# Revit family: ATAG_CV_ketel_Q51_en_Q60_solo
name_source: partatom
category: Mechanical Equipment
revit_build: Autodesk Revit 2014 (Build: 20130308_1515(x64)
units: mm (PartAtom-declared; Revit-internal decimal feet)

## types (2) — shared parameters
BCB_I BaseKeynote = 56.10.10.13.01
BCB_I Beschermingsgraad vlgs. EN 60529 = IPX0D
BCB_I Beschikbare opvoerhoogte pomp CV = 0.00 Pa
BCB_I Gaskeur HR Top = HR Top
BCB_I Gaskeur SV_gaskeurlabel schone verbranding = SV
BCB_I Gewicht (leeg) = 64
BCB_I Rendement volgens EN677 (36/30°C deellast, onderw.) = 109,3
BCB_I Rendement volgens EN677 (80/60°C vollast, onderw.) = 97,3
BCB_V Aansluitdiameter CVr = 35 mm
BCB_V Aansluitdiameter CVv = 35 mm
BCB_V Aansluitdiameter condensafvoer = 24 mm
BCB_V Aansluitdiameter gas = 20 mm
BCB_V Aansluitdiameter luchttoevoer = 80 mm  [stored 0.262467 ft]
BCB_V Aansluitdiameter rookgasafvoer = 80 mm  [stored 0.262467 ft]
BCB_V Luchtinlaat_materiaal = BE Kunststof_zwart
BCB_c1 Debiet = 0 CFM
BCB_c1 Omschrijving = c1_Rookgasafvoer
BCB_c1 Straal = 40 mm  [stored 0.131234 ft]
BCB_c2 Omschrijving = c2_Elektrische voeding
BCB_c3 Debiet = 0.0000 L/s
BCB_c3 Energie_inhoud gas = 0 kWh
BCB_c3 Omschrijving = c3_Gasaansluiting
BCB_c3 Straal = 10 mm  [stored 0.0328084 ft]
BCB_c3 Vermogen = 0 kW
BCB_c4 Omschrijving = c4_CV-toevoer
BCB_c4 Straal = 18 mm  [stored 0.0590551 ft]
BCB_c5 Omschrijving = c5_CV-retour
BCB_c5 Straal = 18 mm  [stored 0.0590551 ft]
BCB_c6 Omschrijving = c6_Condensafvoer
BCB_c6 Straal = 12 mm  [stored 0.0393701 ft]
BCB_c7 Debiet = 0 CFM
BCB_c7 Omschrijving = c7_Luchttoevoer
BCB_c7 Straal = 40 mm  [stored 0.131234 ft]
Default Elevation = 1000 mm  [stored 3.28084 ft]
GTIN-14 = -
IFC_versie = 2x3
IfcExportAs = IfcGasTerminalType
IfcExportType = gasappliance
Manufacturer = ATAG
Model = Q-serie
NL_E Aantal polen = 1
NL_E Arbeidsfactor = 1
NL_E Belastingsklasse = Other
NL_E Belastingssubklasse motor = No
NL_E Schijnbaar vermogen = 0 VA
NL_E Spanning = 230 V
NL_E Vermogen = 0 W
NL_G Breedte = 660 mm  [stored 2.16535 ft]
NL_G Diepte = 385 mm  [stored 1.26312 ft]
NL_G Hoogte = 680 mm  [stored 2.23097 ft]
NL_I Bestelcode = -
NL_M Debiet = 0 CFM
NL_P FBW = 0.5
Type Comments = wandketel
ZZ_Z Aansluiting CV_geen accessoire = NL_M Accessoires aansluitingen CV : Geen
ZZ_Z Aansluiting CVr_X coördinaat = 115 mm
ZZ_Z Aansluiting CVr_Y coördinaat = -143 mm
ZZ_Z Aansluiting CVr_type accessoire = NL_M Accessoires aansluitingen CV : Kraan
ZZ_Z Aansluiting CVv_X coördinaat = -145 mm
ZZ_Z Aansluiting CVv_Y coördinaat = -143 mm
ZZ_Z Aansluiting CVv_type accessoire = NL_M Accessoires aansluitingen CV : Kraan
ZZ_Z Aansluiting gas_X coördinaat = -265 mm
ZZ_Z Aansluiting gas_Y coördinaat = -153 mm
ZZ_Z Aansluiting gas_geen accessoire = NL_M Accessoires aansluitingen gas : Geen
ZZ_Z Aansluiting gas_type accessoire = NL_M Accessoires aansluitingen gas : Kraan
ZZ_Z Aansluiting luchttoevoer_X coördinaat = -165 mm
ZZ_Z Aansluiting luchttoevoer_Y coördinaat = -43 mm
ZZ_Z Aansluiting rookgas_X coördinaat = -165 mm
ZZ_Z Aansluiting rookgas_Y coördinaat = 78 mm
ZZ_Z Aansluiting rookgas_linkerzijde = 495 mm
ZZ_Z Binnendiameter rookgasafvoer = 60 mm  [stored 0.19685 ft]
ZZ_Z Condensafvoer_X coördinaat = 200 mm  [stored 0.656168 ft]
ZZ_Z Condensafvoer_Y coördinaat = -168 mm
ZZ_Z Condensafvoer_accessoire = NL_M Accessoires aansluitingen CV : Geen
ZZ_Z Expansievat_breedte2 = 1 mm  [stored 0.00328084 ft]
ZZ_Z Expansievat_diepte2 = 1 mm  [stored 0.00328084 ft]
ZZ_Z Expansievat_hoogte2 = 1 mm  [stored 0.00328084 ft]
ZZ_Z Expansievatmodule = No
ZZ_Z Halve breedte negatief = -330 mm
fabrikant_artikelcode = -
fabrikant_bibliotheek_versie = v1.0
fabrikant_jaartal = 2014
fabrikant_revisie = -
materiaal = <By Category>
revit_versie = 2014
zero-valued in all types: ZZ_Z Expansievat_breedte, ZZ_Z Expansievat_diepte, ZZ_Z Expansievat_hoogte, ZZ_Z Ketel_afstand

## per-type parameters (varying)
| type | BCB_I Belasting op bovenwaarde CV | BCB_I Belasting op onderwaarde CV | BCB_I Gasverbruik G25 CV (bij 1013 mbar/15°C)_m3/h | BCB_I Modulatiebereik CV (vermogen, 50/30°C) | BCB_I Modulatiebereik CV (vermogen, 80/60°C) |
| Q51S | 51000 W | 45900 W | 5,65 | 9,6 - 48,7 | 8,8 - 44,7 |
| Q60S | 60000 W | 54000 W | 6,56 | 9,6 - 57,3 | 8,8 - 52,5 |

note: column(s) folded — value = type name in every type: BCB_I Type

note: [stored X ft] marks values corroborated as IEEE doubles in the binary element streams (Revit-internal decimal feet)

## geometry (parser evidence)
native form markers: Blend x2, Sweep x50
no freeform markers — native parametric forms only
